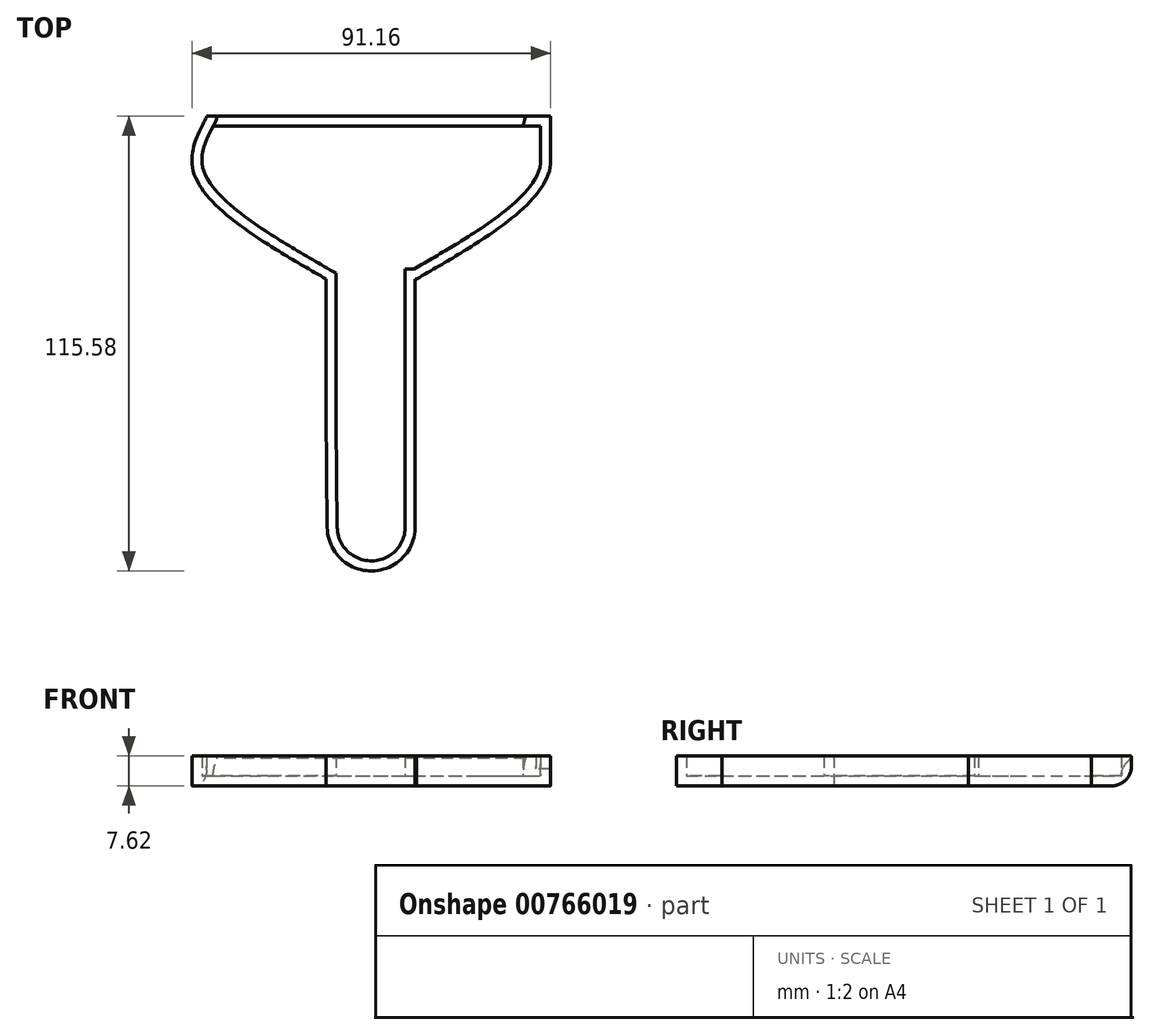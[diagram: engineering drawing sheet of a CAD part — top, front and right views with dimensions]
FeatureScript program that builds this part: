
annotation { "Feature Type Name" : "Feature", "Feature Type Description" : "" }
export const myFeature = defineFeature(function(context is Context, id is Id, definition is map)
    precondition{}
    {
        {
            var Q0;
            Q0=qCreatedBy(makeId("Top.planeOp"),FACE);
            var sketch = newSketch(context, id + "F0", { "sketchPlane" : qUnion([Q0])});
            skArc(sketch, "E0", {"start": v(-11.17, -28.93) * mm, "mid": v(0.22, -39.97) * mm, "end": v(11.17, -28.49) * mm});
            skLineSegment(sketch, "E1", {"start": v(-11.17, -28.93) * mm, "end": v(-11.53, 0) * mm});
            skLineSegment(sketch, "E2", {"start": v(11.17, -28.49) * mm, "end": v(11.17, 0) * mm});
            skLineSegment(sketch, "E3", {"start": v(-11.53, 0) * mm, "end": v(-11.53, 34.19) * mm});
            skLineSegment(sketch, "E4", {"start": v(11.17, 0) * mm, "end": v(11.17, 33.62) * mm});
            skFitSpline(sketch, "E5", {"points": [v(-11.5, 34.19) * mm, v(-45.54, 63.41) * mm, v(-41.85, 75.33) * mm, v(-41.85, 75.61) * mm], "startDerivative": vector(-79.77, 46.02) * mm, "endDerivative": vector(-1.6, 3.7) * mm});
            skFitSpline(sketch, "E6.MirrorCS", {"points": [v(11.5, 34.19) * mm, v(45.54, 63.41) * mm, v(41.85, 75.33) * mm, v(41.85, 75.61) * mm], "startDerivative": vector(79.77, 46.02) * mm, "endDerivative": vector(1.6, 3.7) * mm});
            skLineSegment(sketch, "E7", {"start": v(-41.82, 75.55) * mm, "end": v(41.85, 75.61) * mm});
            skLineSegment(sketch, "E8", {"start": v(-11.17, -28.93) * mm, "end": v(11.17, -28.49) * mm});
            skLineSegment(sketch, "E9", {"start": v(-11.53, 0) * mm, "end": v(11.17, 0) * mm});
            skLineSegment(sketch, "E10", {"start": v(-11.5, 34.19) * mm, "end": v(11.5, 34.19) * mm});
            skLineSegment(sketch, "E11", {"start": v(-28.04, 43.74) * mm, "end": v(28.04, 43.74) * mm});
            skLineSegment(sketch, "E12", {"start": v(-45.54, 63.41) * mm, "end": v(45.54, 63.41) * mm});
            skLineSegment(sketch, "E13.bottom", {"start": v(-11.5, 34.19) * mm, "end": v(11.17, 34.19) * mm});
            skLineSegment(sketch, "E13.top", {"start": v(-11.5, 0) * mm, "end": v(11.17, 0) * mm});
            skLineSegment(sketch, "E13.left", {"start": v(-11.5, 34.19) * mm, "end": v(-11.5, 0) * mm});
            skLineSegment(sketch, "E13.right", {"start": v(11.17, 34.19) * mm, "end": v(11.17, 0) * mm});
            skLineSegment(sketch, "E14.bottom", {"start": v(-41.82, 75.55) * mm, "end": v(45.54, 75.55) * mm});
            skLineSegment(sketch, "E14.top", {"start": v(-41.82, 63.41) * mm, "end": v(45.54, 63.41) * mm});
            skLineSegment(sketch, "E14.left", {"start": v(-41.82, 75.55) * mm, "end": v(-41.82, 63.41) * mm});
            skLineSegment(sketch, "E14.right", {"start": v(45.54, 75.55) * mm, "end": v(45.54, 63.41) * mm});
            skSolve(sketch);
        }
        {
            var Q0;
            Q0 = qSketchRegion(id + "F0", true);
            extrude(context, id + "F1", {"entities" : qUnion([Q0]), "depth" : 7.62 * mm, "offsetDistance" : 25.4 * mm});
        }
        {
            var Q0;
            Q0=makeQuery(id+"F1.opExtrude","CAP_FACE",FACE,{"disambiguationData":[OSD([sQuery(id+"F0.wireOp",EDGE,"E0"),sQuery(id+"F0.wireOp",EDGE,"E1"),sQuery(id+"F0.wireOp",EDGE,"E2"),sQuery(id+"F0.wireOp",EDGE,"E5"),sQuery(id+"F0.wireOp",EDGE,"E6.MirrorCS"),sQuery(id+"F0.wireOp",EDGE,"E7"),sQuery(id+"F0.wireOp",EDGE,"E9"),sQuery(id+"F0.wireOp",EDGE,"E10"),sQuery(id+"F0.wireOp",EDGE,"E13.left"),sQuery(id+"F0.wireOp",EDGE,"E13.right"),sQuery(id+"F0.wireOp",EDGE,"E14.bottom"),sQuery(id+"F0.wireOp",EDGE,"E14.left"),sQuery(id+"F0.wireOp",EDGE,"E14.right")])],"isStart":false});
            shell(context, id + "F2", {"entities" : qUnion([Q0]), "thickness" : 2.54 * mm});
        }
        {
            var Q0;
            Q0=makeQuery(id+"F1.opExtrude","CAP_EDGE",EDGE,{"disambiguationData":[OSD([sQuery(id+"F0.wireOp",EDGE,"E7")])],"isStart":true});
            var Q1;
            {var subQ0=sQuery(id+"F0.wireOp",EDGE,"E7");Q1=makeQuery(id+"F2.opShell","OFFSET_EDGE",EDGE,{"disambiguationData":[OSD([subQ0]),TDD([makeQuery(id+"F1.opExtrude","CAP_EDGE",EDGE,{"disambiguationData":[OSD([subQ0])],"isStart":false})])]});}
            fillet(context, id + "F3", {"entities" : qUnion([Q0, Q1]), "radius" : 5.08 * mm, "tangentPropagation" : true, "allowEdgeOverflow" : false});
        }
    });
